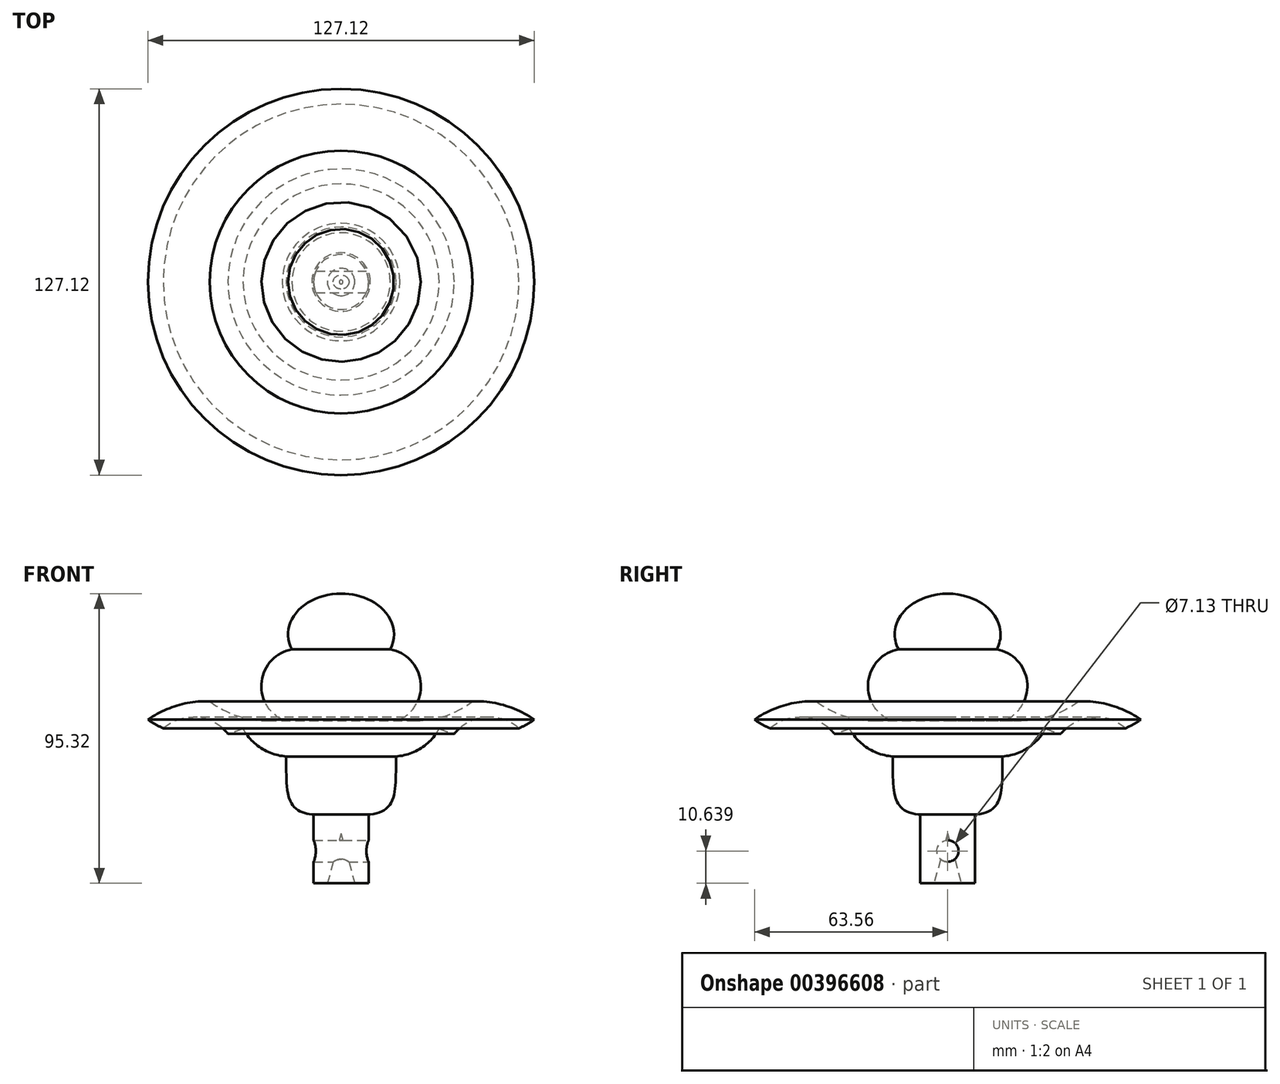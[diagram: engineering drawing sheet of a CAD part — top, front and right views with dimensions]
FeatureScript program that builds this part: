
annotation { "Feature Type Name" : "Feature", "Feature Type Description" : "" }
export const myFeature = defineFeature(function(context is Context, id is Id, definition is map)
    precondition{}
    {
        {
            var Q0;
            Q0=qCreatedBy(makeId("Front.planeOp"),FACE);
            var sketch = newSketch(context, id + "F0", { "sketchPlane" : qUnion([Q0])});
            skEllipticalArc(sketch, "E0", {});
            skLineSegment(sketch, "E1", {"start": v(0, 41.45) * mm, "end": v(0, -37.42) * mm});
            skPoint(sketch, "E1.endSnap0", {"position": v(0, 41.45) * mm});
            skFitSpline(sketch, "E2", {"points": [v(-6.4, 15.63) * mm, v(-16.78, 5.48) * mm, v(-18.07, -12.9) * mm, v(-15.49, -28.71) * mm, v(0, -31.62) * mm], "startDerivative": vector(-53.5, -36.8) * mm, "endDerivative": vector(76.32, 1.17) * mm});
            skLineSegment(sketch, "E3.bottom", {"start": v(-9.64, -31.27) * mm, "end": v(-9.03, -31.27) * mm});
            skLineSegment(sketch, "E3.top", {"start": v(-9.64, -53.87) * mm, "end": v(-9.03, -53.87) * mm});
            skLineSegment(sketch, "E3.left", {"start": v(-9.64, -31.27) * mm, "end": v(-9.64, -53.87) * mm});
            skLineSegment(sketch, "E3.right", {"start": v(-9.03, -31.27) * mm, "end": v(-9.03, -53.87) * mm});
            skLineSegment(sketch, "E4.bottom", {"start": v(-9.03, -53.87) * mm, "end": v(0, -53.87) * mm});
            skLineSegment(sketch, "E4.left", {"start": v(-9.03, -53.87) * mm, "end": v(-9.03, -54.52) * mm});
            skLineSegment(sketch, "E4.right", {"start": v(0, -53.87) * mm, "end": v(0, -54.52) * mm});
            skLineSegment(sketch, "E5", {"start": v(-4.52, -53.87) * mm, "end": v(0, -37.42) * mm});
            skArc(sketch, "E6", {"start": v(-34.4, 6.43) * mm, "mid": v(-34.43, 5.48) * mm, "end": v(-34.4, 4.54) * mm});
            skArc(sketch, "E7", {"start": v(-63.56, 0) * mm, "mid": v(-61.1, -1.54) * mm, "end": v(-58.53, -2.85) * mm});
            skArc(sketch, "E8", {"start": v(-43.23, 6.03) * mm, "mid": v(-53.88, 4.67) * mm, "end": v(-63.56, 0) * mm});
            skPoint(sketch, "E8.startSnap0", {"position": v(-34.4, 6.43) * mm});
            skArc(sketch, "E9.trimOffspring", {"start": v(-32.27, -2.97) * mm, "mid": v(-26.34, -9.35) * mm, "end": v(-18.08, -12.12) * mm});
            skArc(sketch, "E10", {"start": v(-43.23, 6.03) * mm, "mid": v(-31.91, 0.57) * mm, "end": v(-19.36, 0) * mm});
            skArc(sketch, "E11", {"start": v(-16.19, 23.12) * mm, "mid": v(-26.13, 12.7) * mm, "end": v(-19.36, 0) * mm});
            skArc(sketch, "E12", {"start": v(-37.24, -4.7) * mm, "mid": v(-47.49, 0.75) * mm, "end": v(-58.53, -2.85) * mm});
            skArc(sketch, "E13.trimOffspring", {"start": v(-37.24, -4.7) * mm, "mid": v(-34.72, -3.93) * mm, "end": v(-32.27, -2.97) * mm});
            const initialGuessF0  = {"E0": [0, 0.028068024665117264, 1, 0, 0.017421534284949303, 0.013380239428683015, 4.71238898038469, 3.5199983733670392]};
            skSetInitialGuess(sketch, initialGuessF0);
            skSolve(sketch);
        }
        {
            var Q0;
            {var subQ7=sQuery(id+"F0.wireOp",EDGE,"E3.bottom");Q0=makeQuery(id+"F0.imprint","IMPRINT",FACE,{"disambiguationData":[TD([[makeQuery(id+"F0.imprint","IMPRINT",EDGE,{"derivedFrom":subQ7}),1.0]])]});}
            var Q1;
            {var subQ0=sQuery(id+"F0.wireOp",EDGE,"E4.bottom");Q1=makeQuery(id+"F0.imprint","IMPRINT",FACE,{"disambiguationData":[TD([[makeQuery(id+"F0.imprint","IMPRINT",EDGE,{"derivedFrom":subQ0}),1.0]])]});}
            var Q2;
            Q2=sQuery(id+"F0.wireOp",EDGE,"E1");
            revolve(context, id + "F1", {"entities" : qUnion([Q0, Q1]), "axis" : qUnion([Q2]), "revolveType" : RevolveType.FULL});
        }
        {
            var Q0;
            Q0=qCreatedBy(makeId("Right.planeOp"),FACE);
            var sketch = newSketch(context, id + "F2", { "sketchPlane" : qUnion([Q0])});
            skCircle(sketch, "E14", {"center": v(0, -43.23) * mm, "radius": 3.56 * mm});
            skSolve(sketch);
        }
        {
            var Q0;
            Q0 = qSketchRegion(id + "F2", true);
            extrude(context, id + "F3", {"entities" : qUnion([Q0]), "operationType" : NewBodyOperationType.REMOVE, "oppositeDirection" : true, "depth" : 25.4 * mm});
        }
        {
            var Q0;
            Q0 = qSketchRegion(id + "F2", true);
            extrude(context, id + "F4", {"entities" : qUnion([Q0]), "operationType" : NewBodyOperationType.REMOVE, "depth" : 25.4 * mm});
        }
    });
